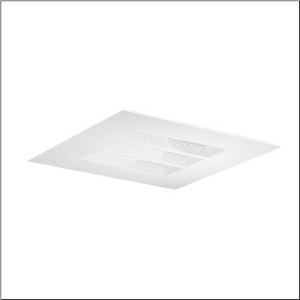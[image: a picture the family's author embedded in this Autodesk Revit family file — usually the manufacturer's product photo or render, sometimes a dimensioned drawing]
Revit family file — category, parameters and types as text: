
# Revit family: taris_r__21_51mt1lv0jhgedb02_8874
name_source: partatom
category: Lighting Fixtures
units: mm (PartAtom-declared; Revit-internal decimal feet)

## family parameters
Cut with Voids When Loaded = No
Host = Face
Light Source = No
Part Type = Normal
Room Calculation Point = No
Round Connector Dimension = Use Diameter
Shared = No

## types (1)
- Taris® 21 (1 x LED, 4620 lm, 31.1 W, 4000K)
    Apparent Load = 31 VA
    CIE Flux Codes = 79 97 100 100 100
    Color Rendering = 80
    Color Temperature = 4000K
    Default Elevation = 1800 mm
    Description = Taris® 21, office luminaire, primary anti-glare with micro louvre, primary optical cover: axial lens, of PMMA, structured, CAT 2 (L<= 1500cd/m²), light emission: direct distribution, primary light characteristic: symmetric, installation type: lay-in mounting, LED rated luminous flux: 4.620 lm, light colour: 840, colour temperature: 4000K, control gear: ECG, with terminal, 3-pole, mains connection: 230V, AC, 50Hz, rated input power: 31W, housing, luminaire housing, of plastic, traffic white (RAL 9016), module: M600, length: 597 mm, width: 597 mm, height: 42mm, protection rating (complete): IP20, insulation class (complete): insulation class I (protective earthing), certification: CE, ENEC, VDE, protection symbol: F, impact resistance: IK02, permissible ambient temperature for indoor applications: 0..+35°C, standard: EN 50419, packaging unit: 1 piece
    Height = 0 mm  [stored 0 ft]
    Lamp = 1 x LED
    Lamp Light Flux = 4620 lm
    Lamp Power = 31.1 W
    Lamp count = 1
    Length = 597 mm
    Luminous efficacy = 149 lm/W
    Manufacturer = Siteco
    ModVariant = No
    Model = 51MT1LV0JHGEDB02
    Mounting Place = Ceiling
    Mounting Type = Recessed
    Number of Poles = 1
    OnlyDefault = Yes
    Power Factor = 1
    Product Name = Taris® 21
    Product group = office luminaire | ceiling recessed
    ProductGroupID = 400
    Protection Class = Protection class I
    Protection Degree = IP 20
    RLX_Detail_Level = 1
    RlxData = <blob elided: 19553 chars, md5=543a7622>
    Socket = socket
    Standby Power = 0 W
    System Light Flux = 4620 lm
    System Power = 31 W
    Type Comments = Product without accessories
    Type Image = l_1004820.jpg
    URL = http://relux.com
    VarID = ---
    Voltage = 0 V
    Weight = 0.00 kg
    Width = 597 mm

note: [stored X ft] marks values corroborated as IEEE doubles in the binary element streams (Revit-internal decimal feet)

## geometry (parser evidence)
native form markers: Blend x4, Sweep x12
no freeform markers — native parametric forms only
